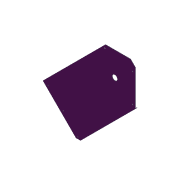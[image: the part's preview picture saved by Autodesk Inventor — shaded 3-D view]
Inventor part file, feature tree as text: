
AUTODESK INVENTOR PART (.ipt)
format: ipt  version: 2012 (Build 160160000, 160)  size: 158,208 bytes
history: native  units: in
note: dims shown in document units (in); Inventor stores cm internally (conversion verified against a paired STEP export)
features: extrude x5, sketch x5, fillet x1
ambient origin geometry x8: Origin, YZ Plane, XZ Plane, XY Plane, X Axis, Y Axis, Z Axis, Center Point
feature tree (11):
  extrude  "Extrusion14"  Depth=8.0in
  extrude  "Extrusion15"  Depth=6.0in
  extrude  "Extrusion16"  TaperAngle=135.0deg  [1 undecoded]
  extrude  "Extrusion17"  Depth=15.0in
  extrude  "Extrusion18"  Depth=20.0in
  fillet  "Fillet1"  Radius=6.25in
  sketch  "Sketch1"  dims[d12=11.0in d14=30.0in d222=8.0in]
  sketch  "Sketch12"  dims[d228=0.5in d229=6.0in]
  sketch  "Sketch13"  dims[d230=1.0in d233=135.0deg]
  sketch  "Sketch14"  dims[d236=0.25in d237=15.0in]
  sketch  "Sketch15"  dims[d238=4.25in d240=20.0in d241=6.25in d242=1.125in d245=0.0625in d246=0.0in d247=11.0in d248=20.0in d249=0.25in d250=1.5in d252=1.0in d253=1.0in d254=0.375in d255=0.125in d256=0.0in d257=0.0625in d258=0.375in d259=0.0in d260=0.125in d261=0.0in d262=1.0in d263=0.375in d264=0.0in d266=0.0625in d267=0.375in d268=0.0in d269=0.0156in]
note: 1 required parameter value undecoded (feature->parameter linkage not recoverable at this tier; creation-order binding heuristic only, values carry confidence <= 0.55)
